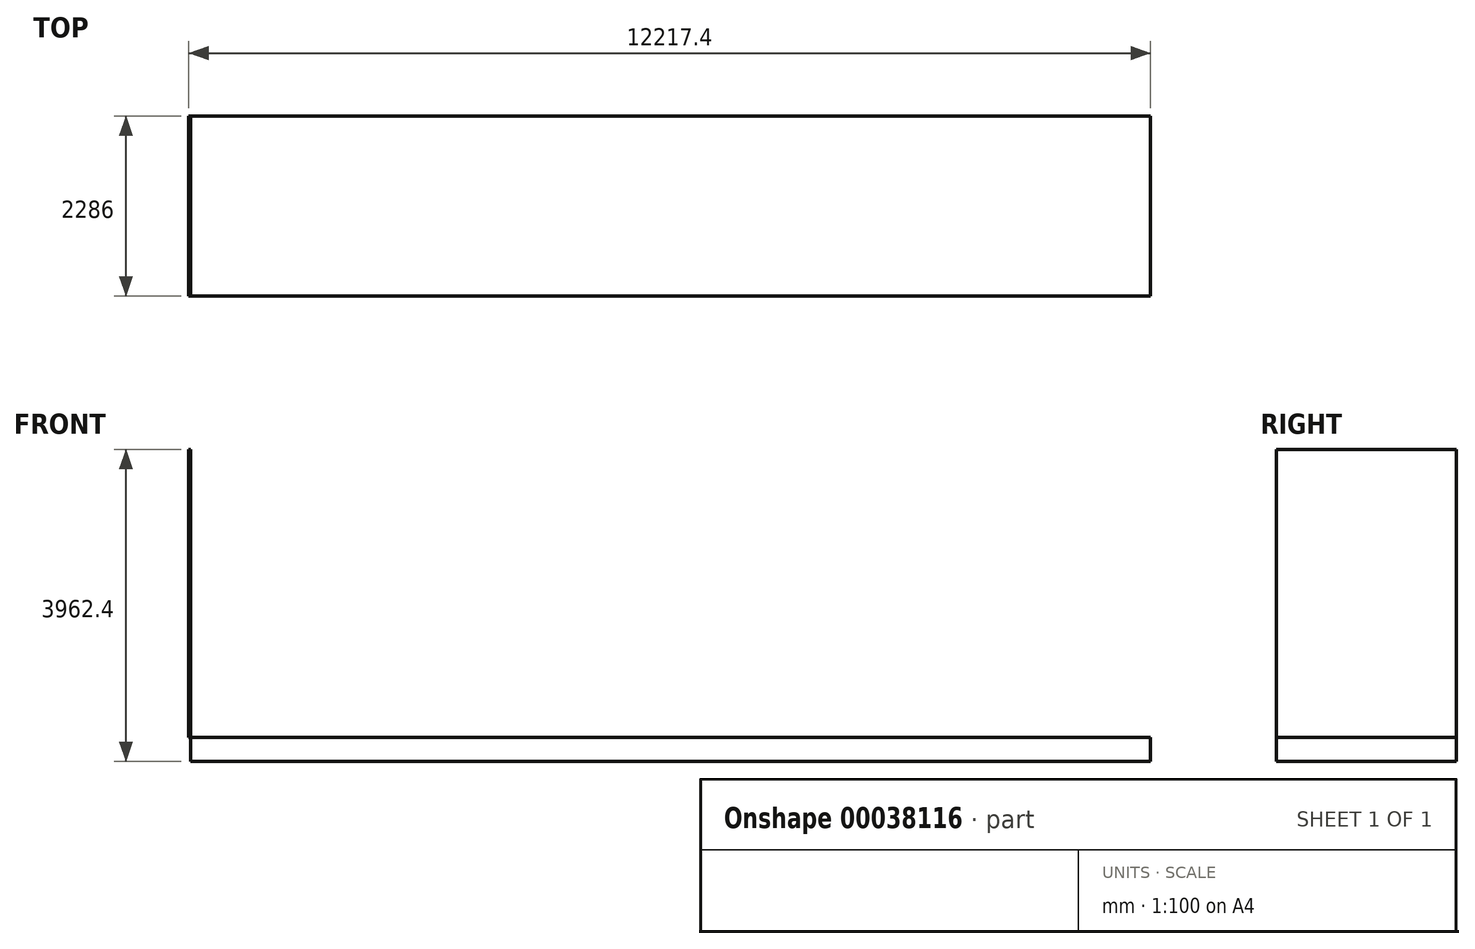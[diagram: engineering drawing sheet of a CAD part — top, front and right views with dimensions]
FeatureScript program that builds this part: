
annotation { "Feature Type Name" : "Feature", "Feature Type Description" : "" }
export const myFeature = defineFeature(function(context is Context, id is Id, definition is map)
    precondition{}
    {
        {
            var Q0;
            Q0=qCreatedBy(makeId("Top.planeOp"),FACE);
            var sketch = newSketch(context, id + "F0", { "sketchPlane" : qUnion([Q0])});
            skLineSegment(sketch, "E0.bottom", {"start": v(0, 0) * mm, "end": v(12192, 0) * mm});
            skLineSegment(sketch, "E0.top", {"start": v(0, 2286) * mm, "end": v(12192, 2286) * mm});
            skLineSegment(sketch, "E0.left", {"start": v(0, 0) * mm, "end": v(0, 2286) * mm});
            skLineSegment(sketch, "E0.right", {"start": v(12192, 0) * mm, "end": v(12192, 2286) * mm});
            skSolve(sketch);
        }
        {
            var Q0;
            Q0=qSketchRegion(id+"F0",true);
            extrude(context, id + "F1", {"entities" : qUnion([Q0]), "oppositeDirection" : true, "depth" : 304.8 * mm});
        }
        {
            var Q0;
            Q0=makeQuery(id+"F1.opExtrude","SWEPT_FACE",FACE,{"disambiguationData":[OSD([sQuery(id+"F0.wireOp",EDGE,"E0.left")])]});
            var sketch = newSketch(context, id + "F2", { "sketchPlane" : qUnion([Q0])});
            skLineSegment(sketch, "E1.bottom", {"start": v(-2286, 0) * mm, "end": v(0, 0) * mm});
            skLineSegment(sketch, "E1.top", {"start": v(-2286, 3657.6) * mm, "end": v(0, 3657.6) * mm});
            skLineSegment(sketch, "E1.left", {"start": v(-2286, 0) * mm, "end": v(-2286, 3657.6) * mm});
            skLineSegment(sketch, "E1.right", {"start": v(0, 0) * mm, "end": v(0, 3657.6) * mm});
            skSolve(sketch);
        }
        {
            var Q0;
            Q0=makeQuery(id+"F2.imprint","IMPRINT",FACE,{"disambiguationData":[TD([[makeQuery(id+"F2.imprint","IMPRINT",EDGE,{"derivedFrom":sQuery(id+"F2.wireOp",EDGE,"E1.bottom")}),-1.0]])]});
            extrude(context, id + "F3", {"entities" : qUnion([Q0]), "depth" : 25.4 * mm});
        }
    });
